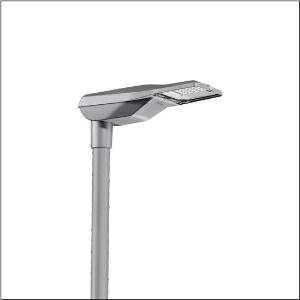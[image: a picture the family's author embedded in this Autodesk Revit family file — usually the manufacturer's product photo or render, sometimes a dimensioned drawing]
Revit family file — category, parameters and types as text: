
# Revit family: streetlight_sl_21_micro___stw1_0a_5xe5e33a08cb_5a2f
name_source: partatom
category: Lighting Fixtures
units: mm (PartAtom-declared; Revit-internal decimal feet)

## family parameters
Cut with Voids When Loaded = No
Host = Face
Light Source = No
Part Type = Normal
Room Calculation Point = No
Round Connector Dimension = Use Diameter
Shared = No

## types (1)
- --- (1 x LED, 2290 lm, 15.8 W, 3000K)
    Apparent Load = 16 VA
    CIE Flux Codes = 38 75 98 100 100
    Color Rendering = 70
    Color Temperature = 3000K
    Default Elevation = 1800 mm
    Description = Streetlight SL 21 micro, mast luminaire, primary light control with lens, of PMMA, primary optical cover: cover, of toughened safety glass, transparent, light distribution: STW1.0a, light emission: direct distribution, primary light characteristic: asymmetric, installation type: side-entry, post-top, LED, 3G 1.5mm², High Power LED, rated luminous flux: 2.290lm, luminous efficacy: 145lm/W, light colour: 730, colour temperature: 3000K, control: flexible luminous flux parameterisation, time-dependent luminous flux control, constant luminous flux control, overheat protection, mains connection: 230..240V, AC, 50/60Hz, connection cable pre-assembled, cable length: 5,5m, wiring characteristics: H07RN-F, start of lifetime: 16W, end of service life: 16W, reduction: 9W, luminaire housing, of diecast aluminium, powder-coated, Siteco® metallic grey (DB 702S), corrosivity category C5 mid according to DIN EN ISO 12944, please order mast flange separately, inclination adjustable: 0°, 5°, 10°, 15°, sealing non-destructively replaceable, multi-level sealing system, length: 528mm, width: 235mm, height: 110mm, mast flange for spigot size: 42mm (side-entry): 5XC10008XM4, 60/48mm (side-entry/post-top): 5XC10108XM2, 76/60mm (side-entry/post-top): 5XC10108XM1, protection rating (complete): IP66, insulation class (complete): insulation class II (safety insulation), certification: CE, ENEC, ENEC+, VDE, impact resistance: IK09, permissible operating ambient temperature for outdoor applications: -40..+50°C, standard-compliant lighting for roads and squares, packaging unit: 1 piece

Light Distribution: STW1.0a
    Height = 110 mm
    Lamp = 1 x LED
    Lamp Light Flux = 2290 lm
    Lamp Power = 15.8 W
    Lamp count = 1
    Length = 528 mm
    Luminous efficacy = 145 lm/W
    Manufacturer = Siteco
    ModVariant = No
    Model = 5XE5E33A08CB
    Number of Poles = 1
    OnlyDefault = Yes
    Power Factor = 1
    Product Name = Streetlight SL 21 micro | STW1.0a
    Product group = mast luminaire | pylon top
    ProductGroupID = 6100
    Protection Class = Protection class II
    Protection Degree = IP 66
    RLX_Detail_Level = 1
    RLX_Emergency_Light_Flux = 0 lm
    RLX_Emergency_Type = 0
    RLX_Emergency_Type_DB = No
    RlxData = <blob elided: 97737 chars, md5=02a16908>
    Socket = socket
    Standby Power = 0 W
    System Light Flux = 2290 lm
    System Power = 16 W
    Type Comments = factory setting: luminous flux: 100 % | Output Level: 100 % | 300 mA
    Type Image = l_1006881.jpg
    URL = http://relux.com
    VarID = @adj_105333
    Voltage = 0 V
    Weight = 0.00 kg
    Width = 235 mm

## geometry (parser evidence)
native form markers: Blend x4, Sweep x11
no freeform markers — native parametric forms only
